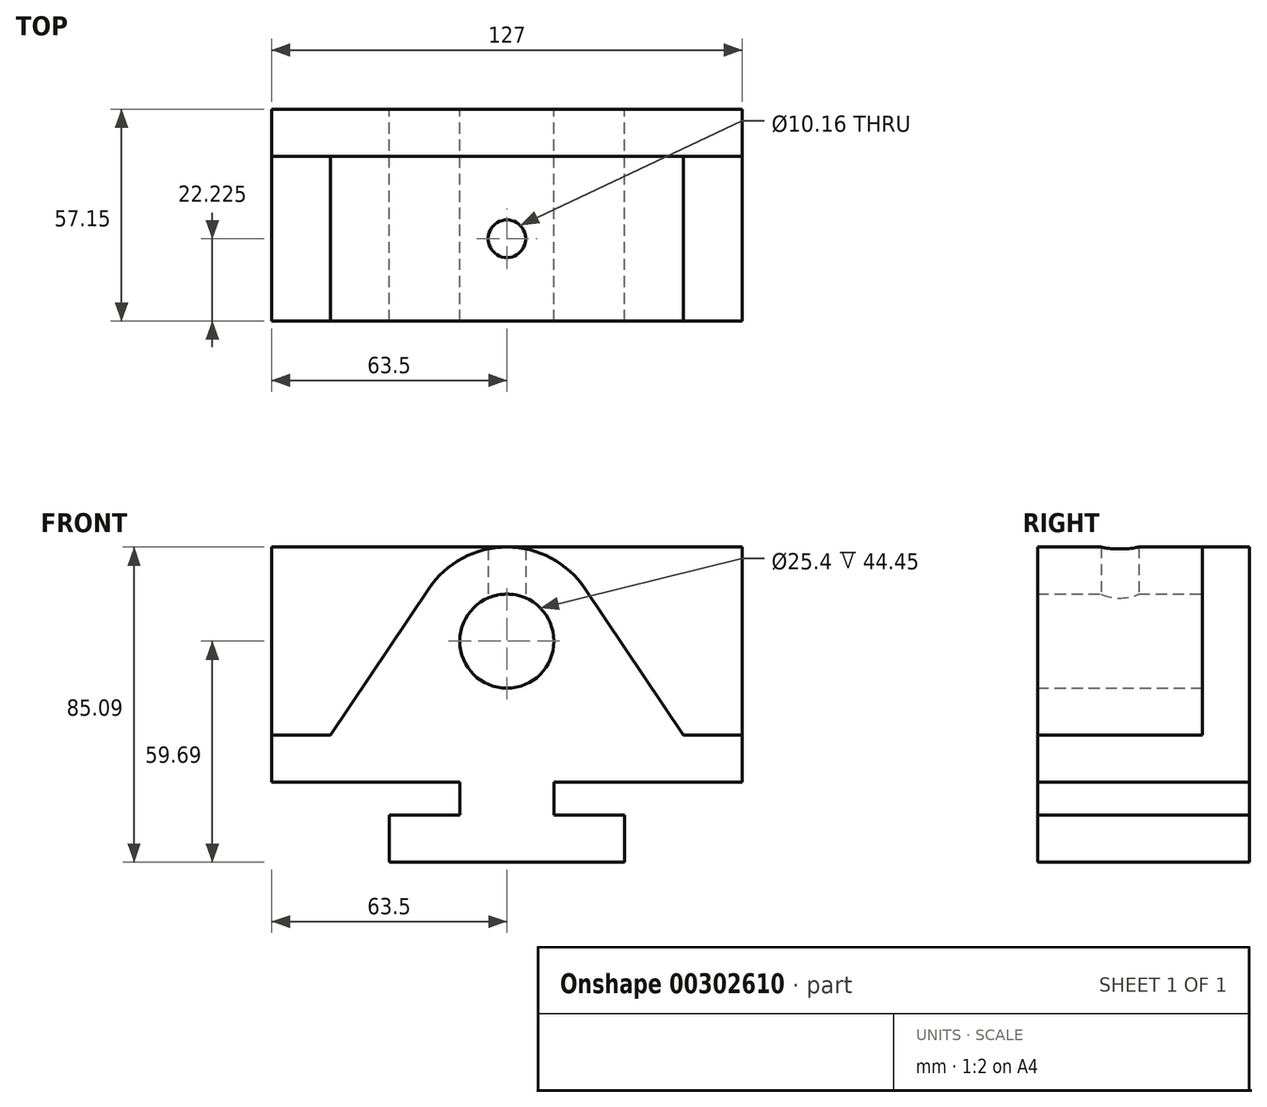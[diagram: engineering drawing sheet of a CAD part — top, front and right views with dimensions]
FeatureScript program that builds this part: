
annotation { "Feature Type Name" : "Feature", "Feature Type Description" : "" }
export const myFeature = defineFeature(function(context is Context, id is Id, definition is map)
    precondition{}
    {
        {
            var Q0;
            Q0=qCreatedBy(makeId("Front.planeOp"),FACE);
            var sketch = newSketch(context, id + "F0", { "sketchPlane" : qUnion([Q0])});
            skLineSegment(sketch, "E0.bottom", {"start": v(-63.5, 31.75) * mm, "end": v(63.5, 31.75) * mm});
            skLineSegment(sketch, "E0.top", {"start": v(-63.5, -31.75) * mm, "end": v(63.5, -31.75) * mm});
            skLineSegment(sketch, "E0.left", {"start": v(-63.5, 31.75) * mm, "end": v(-63.5, -31.75) * mm});
            skLineSegment(sketch, "E0.right", {"start": v(63.5, 31.75) * mm, "end": v(63.5, -31.75) * mm});
            skSolve(sketch);
        }
        {
            var Q0;
            Q0 = qSketchRegion(id + "F0", true);
            extrude(context, id + "F1", {"entities" : qUnion([Q0]), "depth" : 12.7 * mm});
        }
        {
            var Q0;
            Q0=makeQuery(id+"F1.opExtrude","CAP_FACE",FACE,{"disambiguationData":[OSD([sQuery(id+"F0.wireOp",EDGE,"E0.bottom"),sQuery(id+"F0.wireOp",EDGE,"E0.top"),sQuery(id+"F0.wireOp",EDGE,"E0.left"),sQuery(id+"F0.wireOp",EDGE,"E0.right")])],"isStart":false});
            var sketch = newSketch(context, id + "F2", { "sketchPlane" : qUnion([Q0])});
            skLineSegment(sketch, "E1", {"start": v(-63.5, -31.75) * mm, "end": v(-63.5, -19.05) * mm});
            skLineSegment(sketch, "E2", {"start": v(-63.5, -19.05) * mm, "end": v(-47.62, -19.05) * mm});
            skLineSegment(sketch, "E3", {"start": v(-47.62, -19.05) * mm, "end": v(-21.1, 20.5) * mm});
            skArc(sketch, "E4", {"start": v(0, 31.75) * mm, "mid": v(-11.95, 28.76) * mm, "end": v(-21.1, 20.5) * mm});
            skCircle(sketch, "E5", {"center": v(0, 6.35) * mm, "radius": 12.7 * mm});
            skArc(sketch, "E6.MirrorCS", {"start": v(0, 31.75) * mm, "mid": v(11.95, 28.76) * mm, "end": v(21.1, 20.5) * mm});
            skLineSegment(sketch, "E7.MirrorCS", {"start": v(47.63, -19.05) * mm, "end": v(21.1, 20.5) * mm});
            skLineSegment(sketch, "E8.MirrorCS", {"start": v(63.5, -19.05) * mm, "end": v(47.62, -19.05) * mm});
            skLineSegment(sketch, "E9.MirrorCS", {"start": v(63.5, -31.75) * mm, "end": v(63.5, -19.05) * mm});
            skLineSegment(sketch, "E10", {"start": v(-63.5, -31.75) * mm, "end": v(63.5, -31.75) * mm});
            skSolve(sketch);
        }
        {
            var Q0;
            Q0 = qSketchRegion(id + "F2", true);
            extrude(context, id + "F3", {"entities" : qUnion([Q0]), "operationType" : NewBodyOperationType.ADD, "depth" : 44.45 * mm});
        }
        {
            var Q0;
            Q0=qCreatedBy(makeId("Front.planeOp"),FACE);
            var sketch = newSketch(context, id + "F4", { "sketchPlane" : qUnion([Q0])});
            skLineSegment(sketch, "E11", {"start": v(-12.7, -31.75) * mm, "end": v(-12.7, -40.64) * mm});
            skLineSegment(sketch, "E12", {"start": v(-12.7, -40.64) * mm, "end": v(-31.75, -40.64) * mm});
            skLineSegment(sketch, "E13", {"start": v(-31.75, -40.64) * mm, "end": v(-31.75, -53.34) * mm});
            skLineSegment(sketch, "E14", {"start": v(-31.75, -53.34) * mm, "end": v(31.75, -53.34) * mm});
            skLineSegment(sketch, "E15", {"start": v(31.75, -53.34) * mm, "end": v(31.75, -40.64) * mm});
            skLineSegment(sketch, "E16", {"start": v(31.75, -40.64) * mm, "end": v(12.7, -40.64) * mm});
            skLineSegment(sketch, "E17", {"start": v(12.7, -40.64) * mm, "end": v(12.7, -31.75) * mm});
            skLineSegment(sketch, "E18", {"start": v(-12.7, -31.75) * mm, "end": v(12.7, -31.75) * mm});
            skSolve(sketch);
        }
        {
            var Q0;
            Q0 = qSketchRegion(id + "F4", true);
            extrude(context, id + "F5", {"entities" : qUnion([Q0]), "operationType" : NewBodyOperationType.ADD, "depth" : 57.15 * mm});
        }
        {
            var Q0;
            Q0=makeQuery(id+"F1.opExtrude","SWEPT_FACE",FACE,{"disambiguationData":[OSD([sQuery(id+"F0.wireOp",EDGE,"E0.bottom")])]});
            cPlane(context, id + "F6", {"entities" : qUnion([Q0]), "cplaneType" : CPlaneType.OFFSET, "offset" : 25.4 * mm, "oppositeDirection" : true, "width" : 152.4 * mm, "height" : 152.4 * mm});
        }
        {
            var Q0;
            Q0=qCreatedBy(id+"F6.planeOp",FACE);
            var sketch = newSketch(context, id + "F7", { "sketchPlane" : qUnion([Q0])});
            skCircle(sketch, "E19", {"center": v(0, -34.93) * mm, "radius": 5.08 * mm});
            skSolve(sketch);
        }
        {
            var Q0;
            Q0 = qSketchRegion(id + "F7", true);
            extrude(context, id + "F8", {"entities" : qUnion([Q0]), "operationType" : NewBodyOperationType.REMOVE, "depth" : 25.4 * mm});
        }
    });
